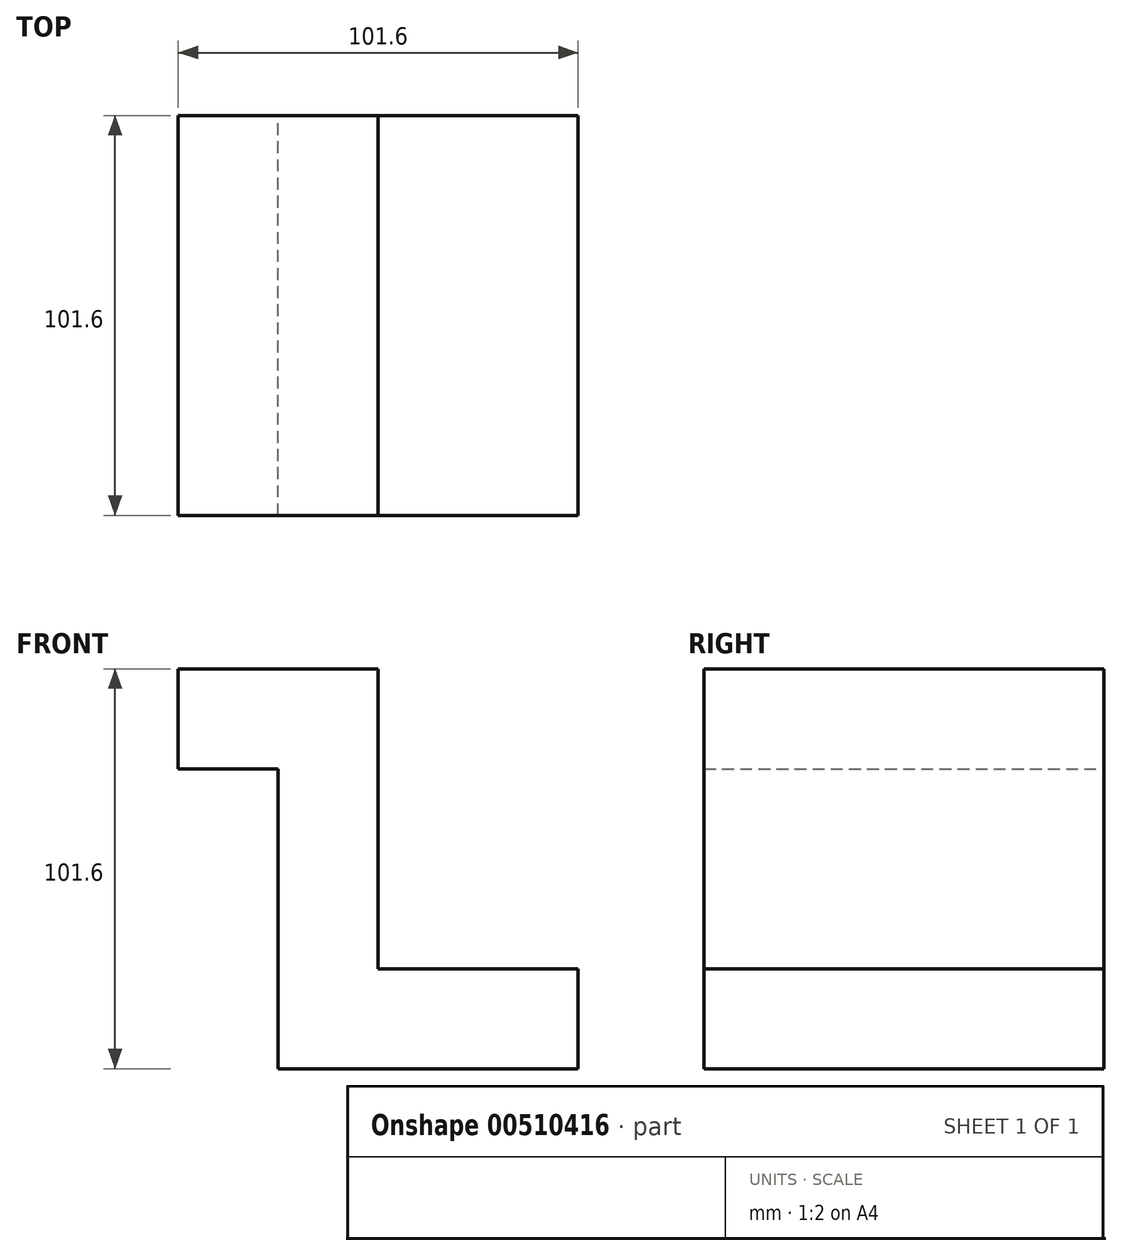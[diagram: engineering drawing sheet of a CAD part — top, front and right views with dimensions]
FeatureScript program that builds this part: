
annotation { "Feature Type Name" : "Feature", "Feature Type Description" : "" }
export const myFeature = defineFeature(function(context is Context, id is Id, definition is map)
    precondition{}
    {
        {
            var Q0;
            Q0=qCreatedBy(makeId("Front.planeOp"),FACE);
            var sketch = newSketch(context, id + "F0", { "sketchPlane" : qUnion([Q0])});
            skLineSegment(sketch, "E0", {"start": v(0, 0) * mm, "end": v(0, 76.2) * mm});
            skLineSegment(sketch, "E1", {"start": v(0, 76.2) * mm, "end": v(-25.4, 76.2) * mm});
            skLineSegment(sketch, "E2", {"start": v(-25.4, 76.2) * mm, "end": v(-25.4, 101.6) * mm});
            skLineSegment(sketch, "E3", {"start": v(-25.4, 101.6) * mm, "end": v(25.4, 101.6) * mm});
            skLineSegment(sketch, "E4", {"start": v(25.4, 101.6) * mm, "end": v(25.4, 25.4) * mm});
            skLineSegment(sketch, "E5", {"start": v(25.4, 25.4) * mm, "end": v(76.2, 25.4) * mm});
            skLineSegment(sketch, "E6", {"start": v(76.2, 25.4) * mm, "end": v(76.2, 0) * mm});
            skLineSegment(sketch, "E7", {"start": v(76.2, 0) * mm, "end": v(0, 0) * mm});
            skSolve(sketch);
        }
        {
            var Q0;
            Q0=makeQuery(id+"F0.imprint","IMPRINT",FACE,{"disambiguationData":[TD([[makeQuery(id+"F0.imprint","IMPRINT",EDGE,{"derivedFrom":sQuery(id+"F0.wireOp",EDGE,"E0")}),-1.0]])]});
            extrude(context, id + "F1", {"entities" : qUnion([Q0]), "depth" : 101.6 * mm});
        }
    });
